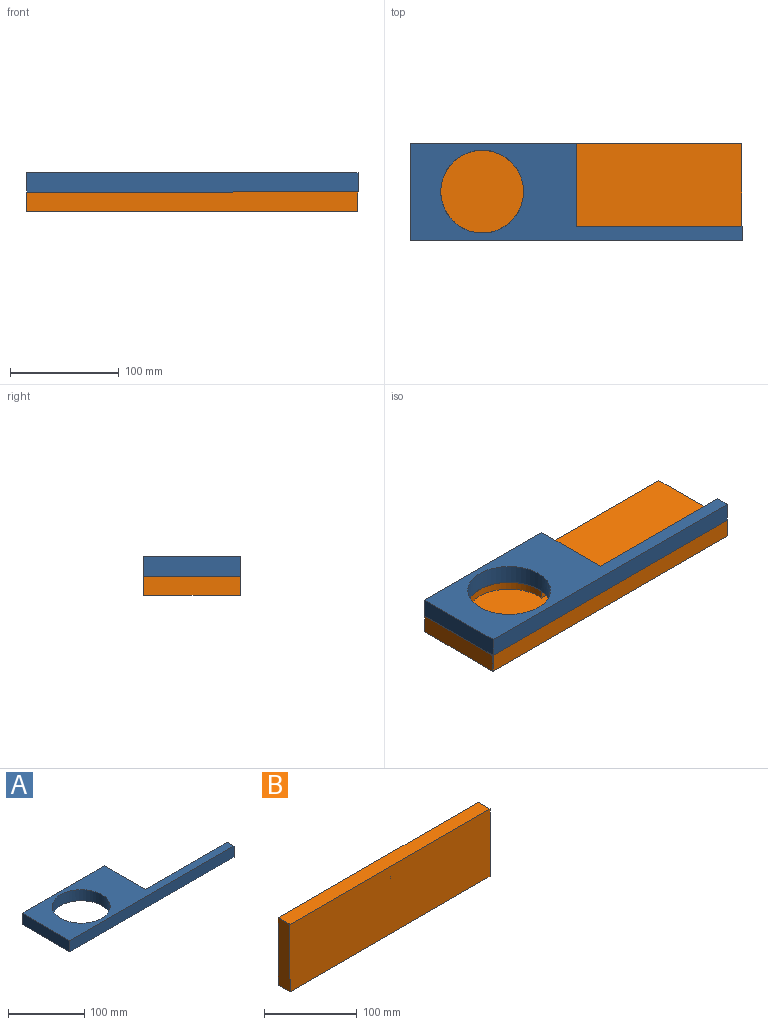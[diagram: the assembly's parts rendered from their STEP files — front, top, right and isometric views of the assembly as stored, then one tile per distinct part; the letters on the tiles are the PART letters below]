
ASSEMBLY  parts=2 mates=1
PART A: 12 faces, bbox 304.8x88.9x17.8 mm
  f0: plane 304.8x88.9mm, normal (0,0,-1), area 10337.6mm2, adj f1,f2,f3,f4,f5,f6,f8,f9
  f1: plane 76.2x17.78mm, normal (1,0,0), area 1251.6mm2, adj f0,f4,f7,f8,f9,f10,f11
  f2: cylinder r=38.1mm len=76.2mm, axis (0,0,1), area 4119.4mm2, adj f0,f7,f9,f10,f11
  f3: plane 17.78x12.7mm, normal (1,0,0), area 225.8mm2, adj f0,f6,f7,f8
  f4: plane 152.4x17.78mm, normal (0,1,0), area 2709.7mm2, adj f0,f1,f5,f7
  f5: plane 88.9x17.78mm, normal (-1,0,0), area 1580.6mm2, adj f0,f4,f6,f7
  f6: plane 304.8x17.78mm, normal (0,-1,0), area 5419.3mm2, adj f0,f3,f5,f7
  f7: plane 304.8x88.9mm, normal (0,0,1), area 10923.5mm2, adj f1,f2,f3,f4,f5,f6,f8
  f8: plane 152.4x17.78mm, normal (0,1,0), area 2709.7mm2, adj f0,f1,f3,f7
  f9: plane 62.57x10.16mm, normal (0,1,0), area 635.7mm2, adj f0,f1,f2,f11
  f10: plane 53.81x10.16mm, normal (0,-1,0), area 546.7mm2, adj f0,f1,f2,f11
  f11: plane 62.57x10.16mm, normal (0,0,-1), area 585.9mm2, adj f1,f2,f9,f10
PART B: 16 faces, bbox 305.4x17.8x88.9 mm
  f0: plane 305.44x88.9mm, normal (0,1,0), area 21206.7mm2, adj f1,f3,f4,f5,f6,f7,f8,f9
  f1: plane 27.93x17.78mm, normal (-1,0,0), area 238.5mm2, adj f0,f2,f10,f11,f14,f15
  f2: plane 10.16x0.01mm, normal (0,0,1), area 0.1mm2, adj f1,f3,f11,f15
  f3: plane 17.78x2.53mm, normal (1,0,0), area 44.9mm2, adj f0,f2,f10,f11,f12
  f4: plane 88.9x17.78mm, normal (-1,0,-0.01), area 1580.6mm2, adj f0,f5,f9,f11
  f5: plane 304.81x17.78mm, normal (0,0,-1), area 5419.5mm2, adj f0,f4,f6,f11
  f6: plane 88.9x17.78mm, normal (1,0,0), area 1580.6mm2, adj f0,f5,f7,f11
  f7: plane 304.8x17.78mm, normal (0,0,1), area 5419.3mm2, adj f0,f6,f8,f11
  f8: plane 17.78x0mm, normal (-1,0,0), area 0mm2, adj f0,f7,f9,f11
  f9: plane 17.78x0.64mm, normal (0,0,1), area 11.3mm2, adj f0,f4,f8,f11
  f10: plane 17.78x0.01mm, normal (0,0,-1), area 0.1mm2, adj f0,f1,f3,f11
  f11: plane 305.44x88.9mm, normal (0,-1,0), area 27125.4mm2, adj f1,f2,f3,f4,f5,f6,f7,f8
  f12: plane 62.57x7.62mm, normal (0,0,-1), area 476.7mm2, adj f0,f3,f13,f15
  f13: cylinder r=38.1mm len=76.2mm, axis (0,1,0), area 1598.1mm2, adj f0,f12,f14,f15
  f14: plane 48.74x7.62mm, normal (0,0,1), area 371.4mm2, adj f0,f1,f13,f15
  f15: plane 124.71x76.2mm, normal (0,1,0), area 5918.7mm2, adj f1,f2,f12,f13,f14
PLACE A rot(axis=(0.26,0.94,0.23),0deg) t=(271.66,25.25,68.78)mm
PLACE B rot(axis=(1,0,0),90deg) t=(298.22,50.15,68.78)mm
MATE planar A.f0 <-> B.f0  axis (0,0,-1) through (53.84,-19.54,68.78)mm
